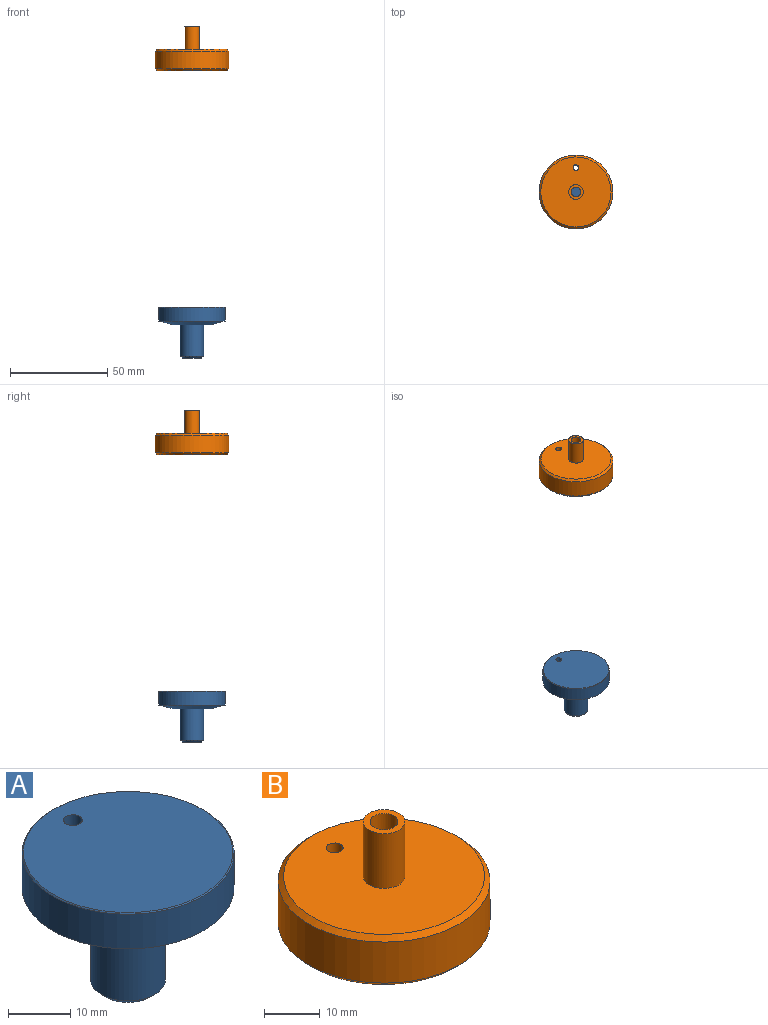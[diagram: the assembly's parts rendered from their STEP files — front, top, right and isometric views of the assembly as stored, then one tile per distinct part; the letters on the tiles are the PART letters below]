
ASSEMBLY  parts=2 mates=1
PART A: 9 faces, bbox 34x34x26 mm
  f0: cylinder r=1.5mm len=8.61mm, axis (0,0,-1), area 77.2mm2, adj f2,f8
  f1: cylinder r=17mm len=34mm, axis (0,0,-1), area 726.3mm2, adj f7,f8
  f2: plane 33.6x33.6mm, normal (0,0,1), area 879.6mm2, adj f0,f7
  f3: plane 19.07x19.07mm, normal (0,0,-1), area 172.6mm2, adj f5,f8
  f4: plane 10x10mm, normal (0,0,-1), area 78.5mm2, adj f6
  f5: cylinder r=6mm len=16mm, axis (0,0,-1), area 603.2mm2, adj f3,f6
  f6: cone r=6mm half-angle=45deg, axis (0,0,1), area 48.9mm2, adj f4,f5
  f7: cone r=16.8mm half-angle=45deg, axis (0,0,-1), area 30mm2, adj f1,f2
  f8: cone r=17mm half-angle=75deg, axis (0,0,1), area 636.9mm2, adj f0,f1,f3
PART B: 11 faces, bbox 38x38x23 mm
  f0: cylinder r=17mm len=34mm, axis (0,0,1), area 854.5mm2, adj f2,f5
  f1: cylinder r=19mm len=38mm, axis (0,0,1), area 1074.4mm2, adj f9,f10
  f2: plane 36x36mm, normal (0,0,-1), area 110mm2, adj f0,f10
  f3: plane 36x36mm, normal (0,0,1), area 966.6mm2, adj f4,f7,f9
  f4: cylinder r=1.5mm len=3mm, axis (0,0,-1), area 28.3mm2, adj f3,f5
  f5: plane 34x34mm, normal (0,0,-1), area 881.2mm2, adj f0,f4,f6
  f6: cylinder r=2.5mm len=15mm, axis (0,0,-1), area 235.6mm2, adj f5,f8
  f7: cylinder r=3.75mm len=12mm, axis (0,0,-1), area 282.7mm2, adj f3,f8
  f8: plane 7.5x7.5mm, normal (0,0,1), area 24.5mm2, adj f6,f7
  f9: cone r=18mm half-angle=45deg, axis (0,0,-1), area 164.4mm2, adj f1,f3
  f10: cone r=19mm half-angle=45deg, axis (0,0,1), area 164.4mm2, adj f1,f2
PLACE A t=(19.06,-13.49,-30.39)mm
PLACE B t=(19.06,-13.49,8.15)mm
MATE slider B.f5 <-> A.f2  axis (0,0,1) through (19.06,-13.59,108.15)mm
